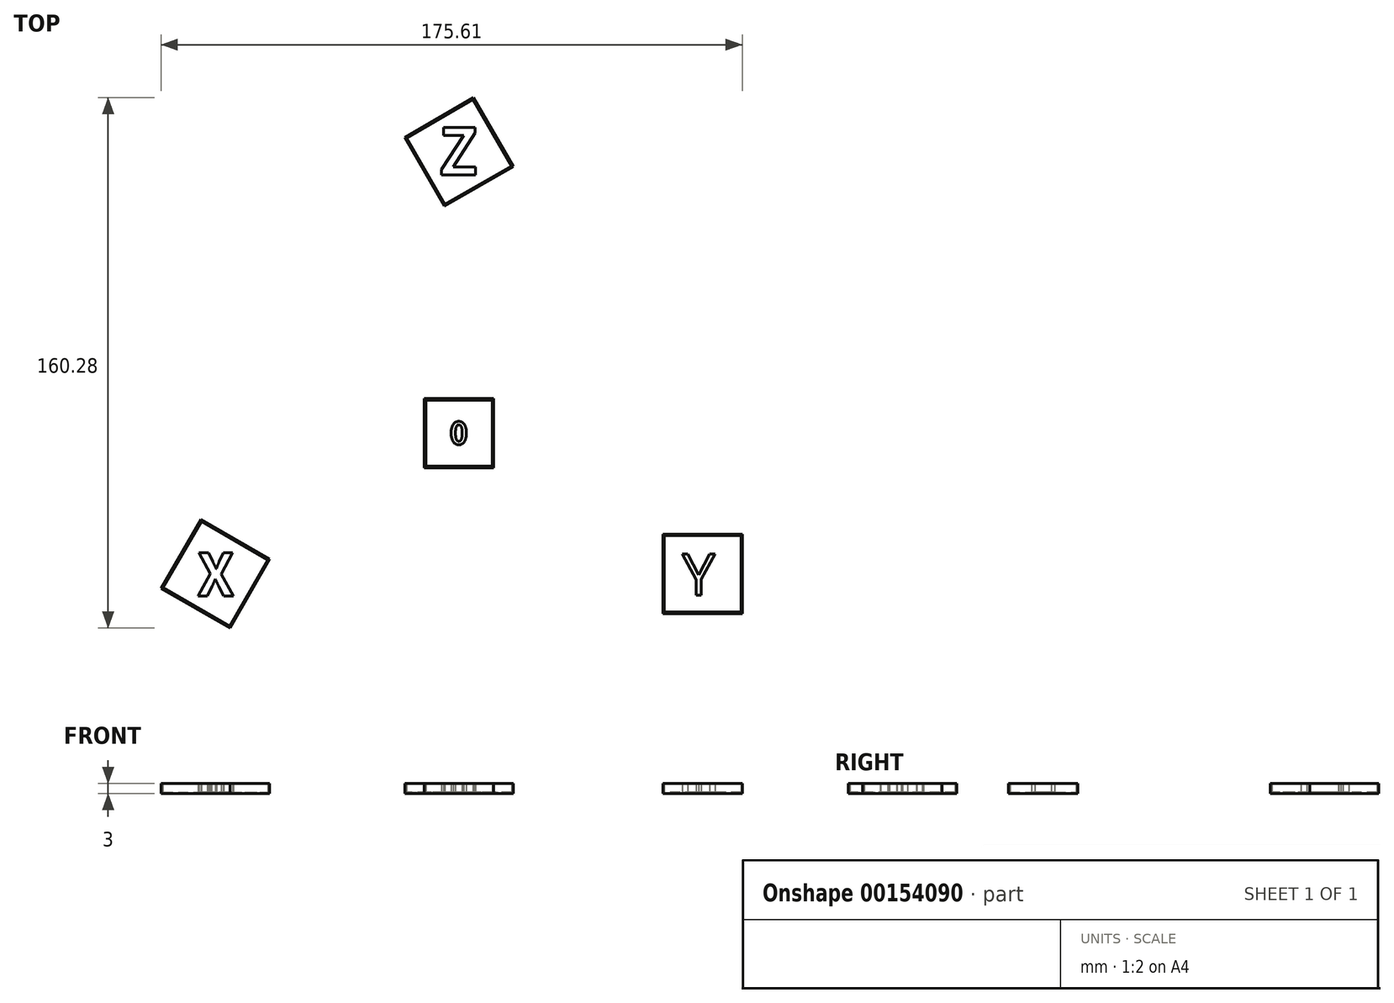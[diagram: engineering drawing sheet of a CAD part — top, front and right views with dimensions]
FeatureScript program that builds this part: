
annotation { "Feature Type Name" : "Feature", "Feature Type Description" : "" }
export const myFeature = defineFeature(function(context is Context, id is Id, definition is map)
    precondition{}
    {
        {
            var Q0;
            Q0=qCreatedBy(makeId("Top.planeOp"),FACE);
            var sketch = newSketch(context, id + "F0", { "sketchPlane" : qUnion([Q0])});
            skCircle(sketch, "E0", {"center": v(0, 0) * mm, "radius": 125 * mm, "construction": true});
            skLineSegment(sketch, "E1.bottom", {"start": v(10, -10) * mm, "end": v(-10, -10) * mm});
            skLineSegment(sketch, "E1.top", {"start": v(10, 10) * mm, "end": v(-10, 10) * mm});
            skLineSegment(sketch, "E1.left", {"start": v(10, -10) * mm, "end": v(10, 10) * mm});
            skLineSegment(sketch, "E1.right", {"start": v(-10, -10) * mm, "end": v(-10, 10) * mm});
            skLineSegment(sketch, "E2.0", {"start": v(10.5, 10.5) * mm, "end": v(-10.5, 10.5) * mm});
            skLineSegment(sketch, "E2.1", {"start": v(10.5, -10.5) * mm, "end": v(10.5, 10.5) * mm});
            skLineSegment(sketch, "E2.2", {"start": v(10.5, -10.5) * mm, "end": v(-10.5, -10.5) * mm});
            skLineSegment(sketch, "E2.3", {"start": v(-10.5, -10.5) * mm, "end": v(-10.5, 10.5) * mm});
            skLineSegment(sketch, "E3", {"start": v(0, 0) * mm, "end": v(0, 125) * mm, "construction": true});
            skLineSegment(sketch, "E4", {"start": v(0, 0) * mm, "end": v(108.25, -62.5) * mm, "construction": true});
            skLineSegment(sketch, "E5", {"start": v(0, 0) * mm, "end": v(-108.25, -62.5) * mm, "construction": true});
            skLineSegment(sketch, "E6", {"start": v(-108.25, -62.5) * mm, "end": v(-106.4, -61.32) * mm, "construction": true});
            skCircle(sketch, "E7", {"center": v(0, 0) * mm, "radius": 85 * mm, "construction": true});
            skLineSegment(sketch, "E8.bottom", {"start": v(85.61, -54.5) * mm, "end": v(61.61, -54.5) * mm});
            skLineSegment(sketch, "E8.top", {"start": v(85.61, -30.5) * mm, "end": v(61.61, -30.5) * mm});
            skLineSegment(sketch, "E8.left", {"start": v(85.61, -54.5) * mm, "end": v(85.61, -30.5) * mm});
            skLineSegment(sketch, "E8.right", {"start": v(61.61, -54.5) * mm, "end": v(61.61, -30.5) * mm});
            skPoint(sketch, "E8.middle", {"position": v(73.61, -42.5) * mm});
            skLineSegment(sketch, "E9.bottom", {"start": v(85.21, -54.1) * mm, "end": v(62.01, -54.1) * mm});
            skLineSegment(sketch, "E9.top", {"start": v(85.21, -30.9) * mm, "end": v(62.01, -30.9) * mm});
            skLineSegment(sketch, "E9.left", {"start": v(85.21, -54.1) * mm, "end": v(85.21, -30.9) * mm});
            skLineSegment(sketch, "E9.right", {"start": v(62.01, -54.1) * mm, "end": v(62.01, -30.9) * mm});
            skLineSegment(sketch, "E10.1.0", {"start": v(4.25, 100.85) * mm, "end": v(15.85, 80.75) * mm});
            skLineSegment(sketch, "E10.1.1", {"start": v(-15.85, 89.25) * mm, "end": v(-4.25, 69.15) * mm});
            skLineSegment(sketch, "E10.1.2", {"start": v(-16.4, 89.4) * mm, "end": v(-4.4, 68.6) * mm});
            skLineSegment(sketch, "E10.1.3", {"start": v(15.85, 80.75) * mm, "end": v(-4.25, 69.15) * mm});
            skPoint(sketch, "E10.1.4", {"position": v(0, 85) * mm});
            skLineSegment(sketch, "E10.1.5", {"start": v(4.25, 100.85) * mm, "end": v(-15.85, 89.25) * mm});
            skLineSegment(sketch, "E10.1.6", {"start": v(4.4, 101.4) * mm, "end": v(16.4, 80.6) * mm});
            skLineSegment(sketch, "E10.1.7", {"start": v(16.4, 80.6) * mm, "end": v(-4.4, 68.6) * mm});
            skLineSegment(sketch, "E10.1.8", {"start": v(4.4, 101.4) * mm, "end": v(-16.4, 89.4) * mm});
            skPoint(sketch, "E10.1.9", {"position": v(0, 85) * mm});
            skLineSegment(sketch, "E10.2.0", {"start": v(-89.46, -46.75) * mm, "end": v(-77.86, -26.65) * mm});
            skLineSegment(sketch, "E10.2.1", {"start": v(-69.37, -58.35) * mm, "end": v(-57.77, -38.25) * mm});
            skLineSegment(sketch, "E10.2.2", {"start": v(-69.22, -58.9) * mm, "end": v(-57.22, -38.1) * mm});
            skLineSegment(sketch, "E10.2.3", {"start": v(-77.86, -26.65) * mm, "end": v(-57.77, -38.25) * mm});
            skPoint(sketch, "E10.2.4", {"position": v(-73.61, -42.5) * mm});
            skLineSegment(sketch, "E10.2.5", {"start": v(-89.46, -46.75) * mm, "end": v(-69.37, -58.35) * mm});
            skLineSegment(sketch, "E10.2.6", {"start": v(-90, -46.9) * mm, "end": v(-78, -26.1) * mm});
            skLineSegment(sketch, "E10.2.7", {"start": v(-78, -26.1) * mm, "end": v(-57.22, -38.1) * mm});
            skLineSegment(sketch, "E10.2.8", {"start": v(-90, -46.9) * mm, "end": v(-69.22, -58.9) * mm});
            skPoint(sketch, "E10.2.9", {"position": v(-73.61, -42.5) * mm});
            skText(sketch, "E11", { "text": "0", "fontName": "NotoSansCJKsc-Bold.otf"});
            skText(sketch, "E12", { "text": "Y", "fontName": "DroidSansMono.ttf"});
            skText(sketch, "E13", { "text": "X", "fontName": "NotoSansCJKsc-Bold.otf"});
            skText(sketch, "E14", { "text": "Z", "fontName": "NotoSansCJKsc-Bold.otf"});
            const initialGuessF0  = {"E11": [-0.00277, -0.00338, 1, 0, 0.00662], "E12": [0.06715, -0.04903, 1, 0, 0.01267], "E13": [-0.07904, -0.04923, 1, 0, 0.0127], "E14": [-0.00616, 0.07797, 1, 0, 0.01402]};
            skSetInitialGuess(sketch, initialGuessF0);
            skSolve(sketch);
        }
        {
            var Q0;
            Q0=makeQuery(id+"F0.imprint","IMPRINT",FACE,{"disambiguationData":[TD([[makeQuery(id+"F0.imprint","IMPRINT",EDGE,{"derivedFrom":sQuery(id+"F0.wireOp",EDGE,"E14.sketch_text.stroke-0")}),1.0]])]});
            var Q1;
            Q1=makeQuery(id+"F0.imprint","IMPRINT",FACE,{"disambiguationData":[TD([[makeQuery(id+"F0.imprint","IMPRINT",EDGE,{"derivedFrom":sQuery(id+"F0.wireOp",EDGE,"E10.1.0")}),1.0]])]});
            var Q2;
            Q2=makeQuery(id+"F0.imprint","IMPRINT",FACE,{"disambiguationData":[TD([[makeQuery(id+"F0.imprint","IMPRINT",EDGE,{"derivedFrom":sQuery(id+"F0.wireOp",EDGE,"E1.bottom")}),1.0]])]});
            var Q3;
            Q3=makeQuery(id+"F0.imprint","IMPRINT",FACE,{"disambiguationData":[TD([[makeQuery(id+"F0.imprint","IMPRINT",EDGE,{"derivedFrom":sQuery(id+"F0.wireOp",EDGE,"E8.bottom")}),-1.0]])]});
            var Q4;
            Q4=makeQuery(id+"F0.imprint","IMPRINT",FACE,{"disambiguationData":[TD([[makeQuery(id+"F0.imprint","IMPRINT",EDGE,{"derivedFrom":sQuery(id+"F0.wireOp",EDGE,"E10.2.0")}),1.0]])]});
            var Q5;
            Q5=makeQuery(id+"F0.imprint","IMPRINT",FACE,{"disambiguationData":[TD([[makeQuery(id+"F0.imprint","IMPRINT",EDGE,{"derivedFrom":sQuery(id+"F0.wireOp",EDGE,"E11.sketch_text.stroke-0")}),1.0]])]});
            var Q6;
            Q6=makeQuery(id+"F0.imprint","IMPRINT",FACE,{"disambiguationData":[TD([[makeQuery(id+"F0.imprint","IMPRINT",EDGE,{"derivedFrom":sQuery(id+"F0.wireOp",EDGE,"E12.sketch_text.stroke-0")}),-1.0]])]});
            var Q7;
            Q7=qSketchRegion(id+"F0",true);
            var Q8;
            Q8=makeQuery(id+"F0.imprint","IMPRINT",FACE,{"disambiguationData":[TD([[makeQuery(id+"F0.imprint","IMPRINT",EDGE,{"derivedFrom":sQuery(id+"F0.wireOp",EDGE,"E13.sketch_text.stroke-0")}),1.0]])]});
            extrude(context, id + "F1", {"entities" : qUnion([Q0, Q1, Q2, Q3, Q4, Q5, Q6, Q7, Q8]), "offsetDistance" : 25 * mm, "depth" : 3 * mm});
        }
        {
            var Q0;
            Q0=makeQuery(id+"F0.imprint","IMPRINT",FACE,{"disambiguationData":[TD([[makeQuery(id+"F0.imprint","IMPRINT",EDGE,{"derivedFrom":sQuery(id+"F0.wireOp",EDGE,"E10.1.0")}),-1.0]])]});
            var Q1;
            Q1=makeQuery(id+"F0.imprint","IMPRINT",FACE,{"disambiguationData":[TD([[makeQuery(id+"F0.imprint","IMPRINT",EDGE,{"derivedFrom":sQuery(id+"F0.wireOp",EDGE,"E10.2.0")}),-1.0]])]});
            var Q2;
            Q2=makeQuery(id+"F0.imprint","IMPRINT",FACE,{"disambiguationData":[TD([[makeQuery(id+"F0.imprint","IMPRINT",EDGE,{"derivedFrom":sQuery(id+"F0.wireOp",EDGE,"E1.bottom")}),-1.0]])]});
            var Q3;
            Q3=makeQuery(id+"F0.imprint","IMPRINT",FACE,{"disambiguationData":[TD([[makeQuery(id+"F0.imprint","IMPRINT",EDGE,{"derivedFrom":sQuery(id+"F0.wireOp",EDGE,"E9.bottom")}),-1.0]])]});
            var Q4;
            Q4=makeQuery(id+"F0.imprint","IMPRINT",FACE,{"disambiguationData":[TD([[makeQuery(id+"F0.imprint","IMPRINT",EDGE,{"derivedFrom":sQuery(id+"F0.wireOp",EDGE,"E11.sketch_text.stroke-4")}),-1.0]])]});
            extrude(context, id + "F2", {"entities" : qUnion([Q0, Q1, Q2, Q3, Q4]), "operationType" : NewBodyOperationType.ADD, "offsetDistance" : 25 * mm, "depth" : .4 * mm});
        }
    });
